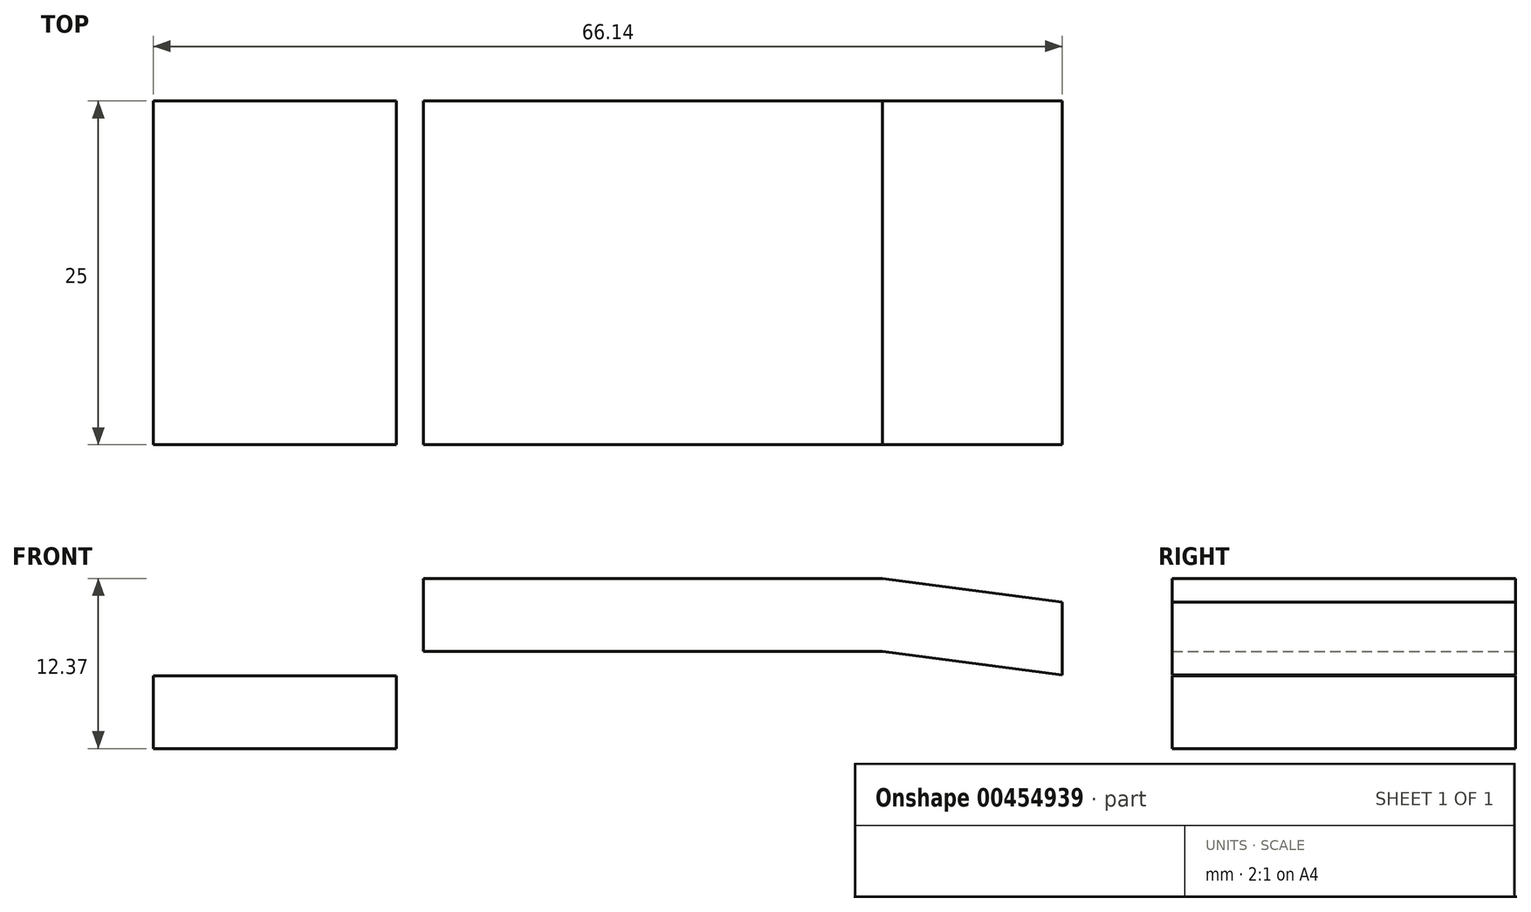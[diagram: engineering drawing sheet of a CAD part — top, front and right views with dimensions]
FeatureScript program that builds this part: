
annotation { "Feature Type Name" : "Feature", "Feature Type Description" : "" }
export const myFeature = defineFeature(function(context is Context, id is Id, definition is map)
    precondition{}
    {
        {
            var Q0;
            Q0=qCreatedBy(makeId("Front.planeOp"),FACE);
            var sketch = newSketch(context, id + "F0", { "sketchPlane" : qUnion([Q0])});
            skLineSegment(sketch, "E0.bottom", {"start": v(-6.41, -9.72) * mm, "end": v(-24.11, -9.72) * mm});
            skLineSegment(sketch, "E0.top", {"start": v(-6.41, -4.42) * mm, "end": v(-24.11, -4.42) * mm});
            skLineSegment(sketch, "E0.left", {"start": v(-6.41, -9.72) * mm, "end": v(-6.41, -4.42) * mm});
            skLineSegment(sketch, "E0.right", {"start": v(-24.11, -9.72) * mm, "end": v(-24.11, -4.42) * mm});
            skPoint(sketch, "E0.middle", {"position": v(-15.26, -7.07) * mm});
            skLineSegment(sketch, "E1.bottom", {"start": v(28.94, -2.65) * mm, "end": v(-4.46, -2.65) * mm});
            skLineSegment(sketch, "E1.top", {"start": v(28.94, 2.65) * mm, "end": v(-4.46, 2.65) * mm});
            skLineSegment(sketch, "E1.left", {"start": v(28.94, -2.65) * mm, "end": v(28.94, 2.65) * mm});
            skLineSegment(sketch, "E1.right", {"start": v(-4.46, -2.65) * mm, "end": v(-4.46, 2.65) * mm});
            skPoint(sketch, "E1.middle", {"position": v(12.24, 0) * mm});
            skLineSegment(sketch, "E2", {"start": v(28.94, 2.65) * mm, "end": v(42.03, 0.95) * mm});
            skLineSegment(sketch, "E3", {"start": v(28.94, -2.65) * mm, "end": v(42.03, -4.35) * mm});
            skLineSegment(sketch, "E4", {"start": v(42.03, 0.95) * mm, "end": v(42.03, -4.35) * mm});
            skLineSegment(sketch, "E5.bottom", {"start": v(42.03, -4.35) * mm, "end": v(48.83, -4.35) * mm});
            skLineSegment(sketch, "E5.top", {"start": v(42.03, -1.35) * mm, "end": v(48.83, -1.35) * mm});
            skLineSegment(sketch, "E5.left", {"start": v(42.03, -4.35) * mm, "end": v(42.03, -1.35) * mm});
            skLineSegment(sketch, "E5.right", {"start": v(48.83, -4.35) * mm, "end": v(48.83, -1.35) * mm});
            skLineSegment(sketch, "E6.bottom", {"start": v(-4.46, 2.65) * mm, "end": v(4.64, 2.65) * mm});
            skLineSegment(sketch, "E6.top", {"start": v(-4.46, -9.15) * mm, "end": v(4.64, -9.15) * mm});
            skLineSegment(sketch, "E6.left", {"start": v(-4.46, 2.65) * mm, "end": v(-4.46, -9.15) * mm});
            skLineSegment(sketch, "E6.right", {"start": v(4.64, 2.65) * mm, "end": v(4.64, -9.15) * mm});
            skLineSegment(sketch, "E7", {"start": v(4.64, -9.15) * mm, "end": v(-6.36, -9.15) * mm});
            skLineSegment(sketch, "E8", {"start": v(-4.46, 2.65) * mm, "end": v(-13.54, -4.4) * mm});
            skLineSegment(sketch, "E9", {"start": v(-43.05, 4.33) * mm, "end": v(-33.05, 4.33) * mm});
            skSolve(sketch);
        }
        {
            var Q0;
            Q0=makeQuery(id+"F0.imprint","IMPRINT",FACE,{"disambiguationData":[TD([[makeQuery(id+"F0.imprint","IMPRINT",EDGE,{"derivedFrom":sQuery(id+"F0.wireOp",EDGE,"E0.bottom")}),-1.0]])]});
            extrude(context, id + "F1", {"entities" : qUnion([Q0]), "endBound" : BoundingType.SYMMETRIC, "depth" : 25 * mm});
        }
        {
            var Q0;
            {var subQ5=sQuery(id+"F0.wireOp",EDGE,"E6.bottom");Q0=makeQuery(id+"F0.imprint","IMPRINT",FACE,{"disambiguationData":[TD([[makeQuery(id+"F0.imprint","IMPRINT",EDGE,{"derivedFrom":subQ5}),-1.0]])]});}
            var Q1;
            {var subQ4=sQuery(id+"F0.wireOp",EDGE,"E1.top");Q1=makeQuery(id+"F0.imprint","IMPRINT",FACE,{"disambiguationData":[TD([[makeQuery(id+"F0.imprint","IMPRINT",EDGE,{"derivedFrom":subQ4}),1.0]])]});}
            extrude(context, id + "F2", {"entities" : qUnion([Q0, Q1]), "endBound" : BoundingType.SYMMETRIC, "depth" : 25 * mm});
        }
        {
            var Q0;
            {var subQ4=sQuery(id+"F0.wireOp",EDGE,"E1.top");Q0=makeQuery(id+"F0.imprint","IMPRINT",FACE,{"disambiguationData":[TD([[makeQuery(id+"F0.imprint","IMPRINT",EDGE,{"derivedFrom":subQ4}),1.0]])]});}
            var Q1;
            Q1=makeQuery(id+"F0.imprint","IMPRINT",FACE,{"disambiguationData":[TD([[makeQuery(id+"F0.imprint","IMPRINT",EDGE,{"derivedFrom":sQuery(id+"F0.wireOp",EDGE,"E1.left")}),-1.0]])]});
            extrude(context, id + "F3", {"entities" : qUnion([Q0, Q1]), "operationType" : NewBodyOperationType.ADD, "endBound" : BoundingType.SYMMETRIC, "depth" : 25 * mm});
        }
    });
